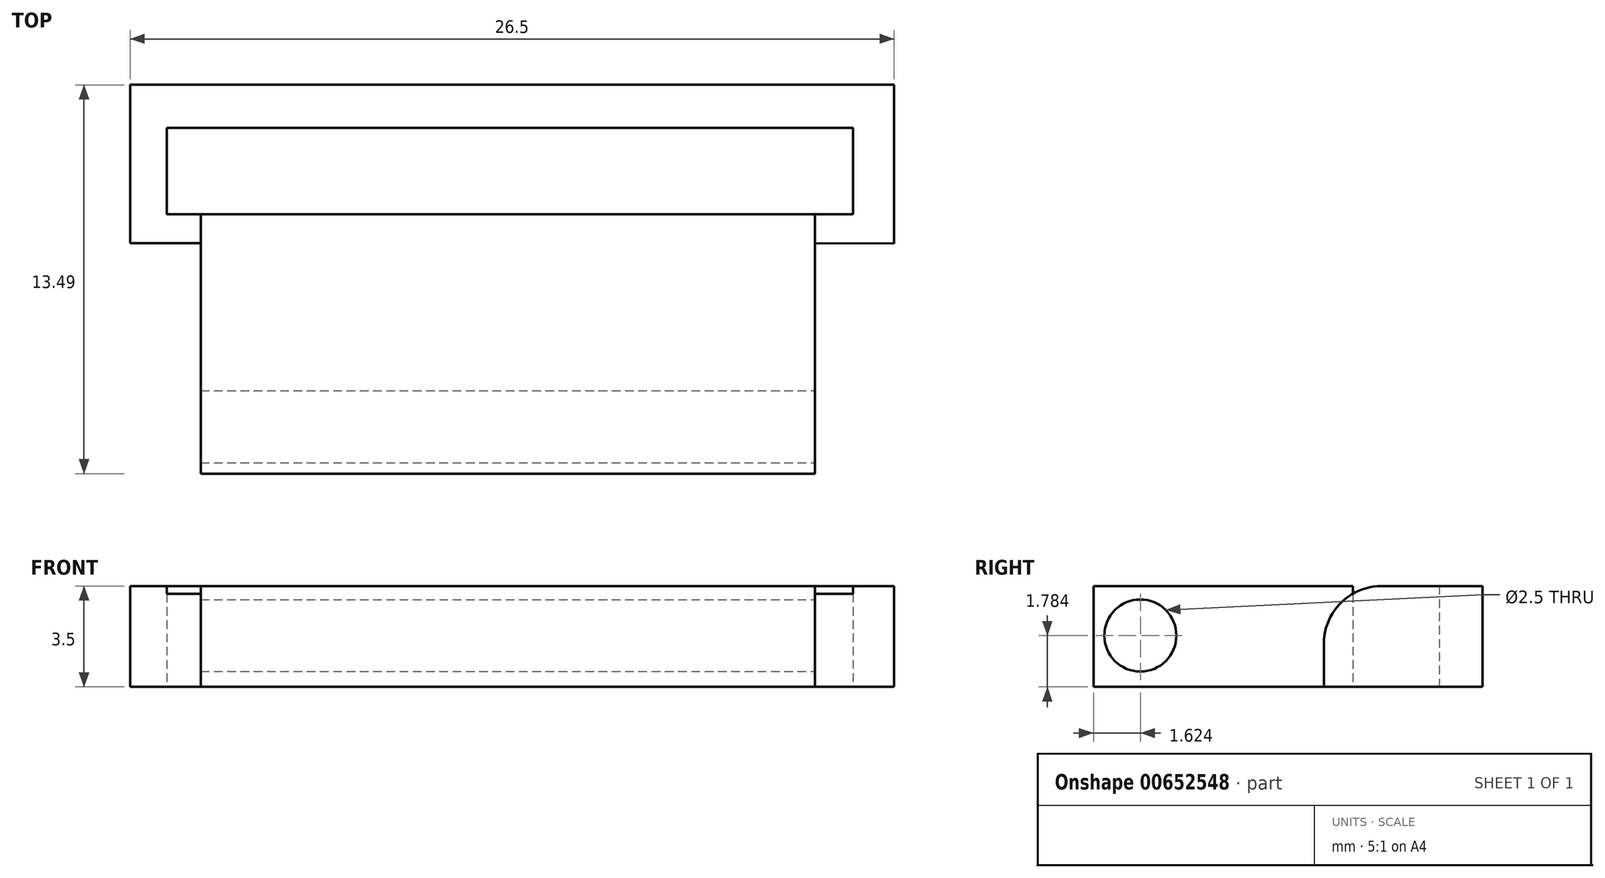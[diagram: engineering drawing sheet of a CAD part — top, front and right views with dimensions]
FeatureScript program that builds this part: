
annotation { "Feature Type Name" : "Feature", "Feature Type Description" : "" }
export const myFeature = defineFeature(function(context is Context, id is Id, definition is map)
    precondition{}
    {
        {
            var Q0;
            Q0=qCreatedBy(makeId("Top.planeOp"),FACE);
            var sketch = newSketch(context, id + "F0", { "sketchPlane" : qUnion([Q0])});
            skLineSegment(sketch, "E0.bottom", {"start": v(11.3, -3.8) * mm, "end": v(-10, -3.8) * mm});
            skLineSegment(sketch, "E0.left", {"start": v(11.3, -3.8) * mm, "end": v(11.3, 4.2) * mm});
            skLineSegment(sketch, "E0.right", {"start": v(-10, -3.8) * mm, "end": v(-10, 4.2) * mm});
            skLineSegment(sketch, "E1.bottom", {"start": v(-12.44, 9.7) * mm, "end": v(14.06, 9.7) * mm});
            skLineSegment(sketch, "E1.left", {"start": v(-12.44, 9.7) * mm, "end": v(-12.44, 4.2) * mm});
            skLineSegment(sketch, "E1.right", {"start": v(14.06, 9.7) * mm, "end": v(14.06, 4.19) * mm});
            skLineSegment(sketch, "E2.bottom", {"start": v(12.63, 5.2) * mm, "end": v(-11.17, 5.2) * mm});
            skLineSegment(sketch, "E2.top", {"start": v(12.63, 8.2) * mm, "end": v(-11.17, 8.2) * mm});
            skLineSegment(sketch, "E2.left", {"start": v(12.63, 5.2) * mm, "end": v(12.63, 8.2) * mm});
            skLineSegment(sketch, "E2.right", {"start": v(-11.17, 5.2) * mm, "end": v(-11.17, 8.2) * mm});
            skLineSegment(sketch, "E3", {"start": v(14.06, 4.19) * mm, "end": v(11.3, 4.2) * mm});
            skLineSegment(sketch, "E4", {"start": v(-12.44, 4.2) * mm, "end": v(-10, 4.2) * mm});
            skLineSegment(sketch, "E5", {"start": v(11.69, 5.2) * mm, "end": v(11.69, 4.2) * mm});
            skLineSegment(sketch, "E6", {"start": v(-10.38, 5.2) * mm, "end": v(-10.38, 4.2) * mm});
            skPoint(sketch, "E6.endSnap0", {"position": v(-11.22, 4.2) * mm});
            skSolve(sketch);
        }
        {
            var Q0;
            Q0=makeQuery(id+"F0.imprint","IMPRINT",FACE,{"disambiguationData":[TD([[makeQuery(id+"F0.imprint","IMPRINT",EDGE,{"derivedFrom":sQuery(id+"F0.wireOp",EDGE,"E0.bottom")}),-1.0]])]});
            var Q1;
            Q1=makeQuery(id+"F0.imprint","IMPRINT",FACE,{"disambiguationData":[TD([[makeQuery(id+"F0.imprint","IMPRINT",EDGE,{"derivedFrom":sQuery(id+"F0.wireOp",EDGE,"E1.bottom")}),-1.0]])]});
            extrude(context, id + "F1", {"entities" : qUnion([Q0, Q1]), "depth" : 3.5 * mm, "offsetDistance" : 25 * mm});
        }
        {
            var Q0;
            Q0=qCreatedBy(makeId("Right.planeOp"),FACE);
            var sketch = newSketch(context, id + "F2", { "sketchPlane" : qUnion([Q0])});
            skCircle(sketch, "E7", {"center": v(-2.18, 1.78) * mm, "radius": 1.25 * mm});
            skSolve(sketch);
        }
        {
            var Q0;
            Q0 = qSketchRegion(id + "F2", true);
            var Q1;
            Q1=sQuery(id+"F2.wireOp",EDGE,"E7");
            extrude(context, id + "F3", {"entities" : qUnion([Q0]), "operationType" : NewBodyOperationType.REMOVE, "surfaceEntities" : qUnion([Q1]), "oppositeDirection" : true, "depth" : 25 * mm, "offsetDistance" : 25 * mm, "hasSecondDirection" : true, "secondDirectionOppositeDirection" : false, "secondDirectionDepth" : 25 * mm});
        }
        {
            var Q0;
            Q0=makeQuery(id+"F1.opExtrude","CAP_EDGE",EDGE,{"disambiguationData":[OSD([sQuery(id+"F0.wireOp",EDGE,"E3")])],"isStart":false});
            var Q1;
            Q1=makeQuery(id+"F1.opExtrude","CAP_EDGE",EDGE,{"disambiguationData":[OSD([sQuery(id+"F0.wireOp",EDGE,"E4")])],"isStart":false});
            fillet(context, id + "F4", {"entities" : qUnion([Q0, Q1]), "radius" : 2 * mm, "tangentPropagation" : true, "allowEdgeOverflow" : false});
        }
    });
